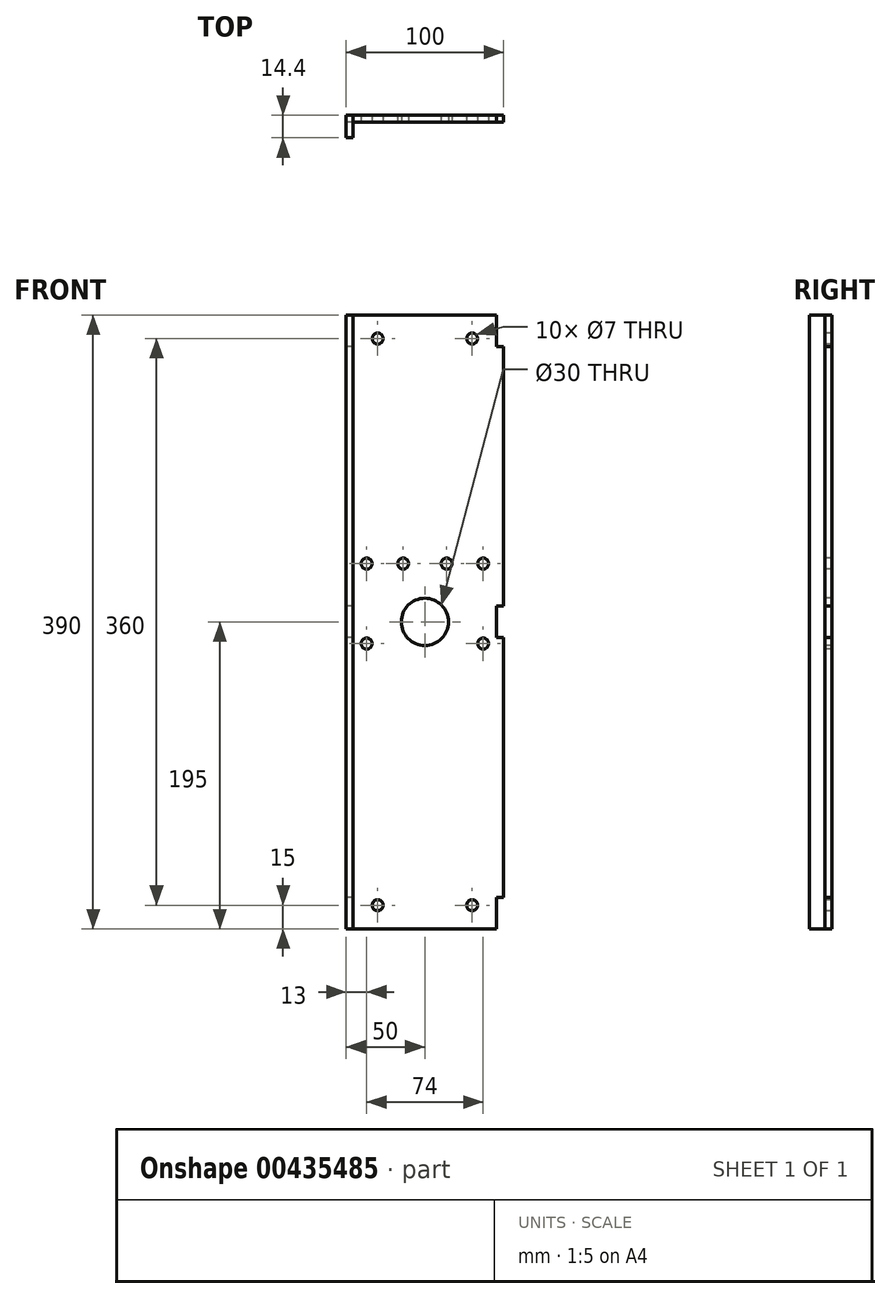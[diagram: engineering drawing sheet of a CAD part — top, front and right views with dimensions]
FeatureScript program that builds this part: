
annotation { "Feature Type Name" : "Feature", "Feature Type Description" : "" }
export const myFeature = defineFeature(function(context is Context, id is Id, definition is map)
    precondition{}
    {
        {
            assignVariable(context, id + "F0", {"name" : "t", "anyValue" : 4.4 * mm});
        }
        {
            var Q0;
            Q0=qCreatedBy(makeId("Front.planeOp"),FACE);
            var sketch = newSketch(context, id + "F1", { "sketchPlane" : qUnion([Q0])});
            skLineSegment(sketch, "E0", {"start": v(0, 0) * mm, "end": v(-45.6, 0) * mm});
            skLineSegment(sketch, "E1", {"start": v(-45.6, 0) * mm, "end": v(-45.6, 20) * mm});
            skLineSegment(sketch, "E2", {"start": v(-45.6, 20) * mm, "end": v(-50, 20) * mm});
            skLineSegment(sketch, "E3", {"start": v(-50, 20) * mm, "end": v(-50, 185) * mm});
            skLineSegment(sketch, "E4", {"start": v(-50, 185) * mm, "end": v(-45.6, 185) * mm});
            skLineSegment(sketch, "E5", {"start": v(-45.6, 185) * mm, "end": v(-45.6, 205) * mm});
            skLineSegment(sketch, "E6", {"start": v(-45.6, 205) * mm, "end": v(-50, 205) * mm});
            skLineSegment(sketch, "E7", {"start": v(-50, 205) * mm, "end": v(-50, 370) * mm});
            skLineSegment(sketch, "E8", {"start": v(-50, 370) * mm, "end": v(-45.6, 370) * mm});
            skLineSegment(sketch, "E9", {"start": v(-45.6, 370) * mm, "end": v(-45.6, 390) * mm});
            skLineSegment(sketch, "E10", {"start": v(-45.6, 390) * mm, "end": v(0, 390) * mm});
            skLineSegment(sketch, "E11", {"start": v(0, 390) * mm, "end": v(45.6, 390) * mm});
            skLineSegment(sketch, "E12", {"start": v(45.6, 390) * mm, "end": v(45.6, 370) * mm});
            skLineSegment(sketch, "E13", {"start": v(45.6, 370) * mm, "end": v(50, 370) * mm});
            skLineSegment(sketch, "E14", {"start": v(50, 370) * mm, "end": v(50, 205) * mm});
            skLineSegment(sketch, "E15", {"start": v(50, 205) * mm, "end": v(45.6, 205) * mm});
            skLineSegment(sketch, "E16", {"start": v(45.6, 205) * mm, "end": v(45.6, 185) * mm});
            skLineSegment(sketch, "E17", {"start": v(45.6, 185) * mm, "end": v(50, 185) * mm});
            skLineSegment(sketch, "E18", {"start": v(50, 185) * mm, "end": v(50, 20) * mm});
            skLineSegment(sketch, "E19", {"start": v(50, 20) * mm, "end": v(45.6, 20) * mm});
            skLineSegment(sketch, "E20", {"start": v(45.6, 20) * mm, "end": v(45.6, 0) * mm});
            skLineSegment(sketch, "E21", {"start": v(45.6, 0) * mm, "end": v(0, 0) * mm});
            skCircle(sketch, "E22", {"center": v(0, 195) * mm, "radius": 15 * mm});
            skLineSegment(sketch, "E23", {"start": v(0, 195) * mm, "end": v(37, 195) * mm, "construction": true});
            skLineSegment(sketch, "E24", {"start": v(37, 195) * mm, "end": v(37, 232) * mm, "construction": true});
            skCircle(sketch, "E25", {"center": v(37, 232) * mm, "radius": 3.5 * mm});
            skLineSegment(sketch, "E26", {"start": v(37, 232) * mm, "end": v(37, 181.2) * mm, "construction": true});
            skLineSegment(sketch, "E27", {"start": v(37, 232) * mm, "end": v(-13.8, 232) * mm, "construction": true});
            skCircle(sketch, "E28", {"center": v(37, 181.2) * mm, "radius": 3.5 * mm});
            skCircle(sketch, "E29", {"center": v(-13.8, 232) * mm, "radius": 3.5 * mm});
            skLineSegment(sketch, "E30", {"start": v(0, 195) * mm, "end": v(-37, 195) * mm, "construction": true});
            skLineSegment(sketch, "E31", {"start": v(-37, 195) * mm, "end": v(-37, 232) * mm, "construction": true});
            skCircle(sketch, "E32", {"center": v(-37, 232) * mm, "radius": 3.5 * mm});
            skLineSegment(sketch, "E33", {"start": v(-37, 232) * mm, "end": v(-37, 181.2) * mm, "construction": true});
            skLineSegment(sketch, "E34", {"start": v(-37, 232) * mm, "end": v(13.8, 232) * mm, "construction": true});
            skCircle(sketch, "E35", {"center": v(-37, 181.2) * mm, "radius": 3.5 * mm});
            skCircle(sketch, "E36", {"center": v(13.8, 232) * mm, "radius": 3.5 * mm});
            skLineSegment(sketch, "E37", {"start": v(0, 0) * mm, "end": v(0, 15) * mm});
            skLineSegment(sketch, "E38", {"start": v(0, 15) * mm, "end": v(30, 15) * mm, "construction": true});
            skLineSegment(sketch, "E39", {"start": v(0, 15) * mm, "end": v(-30, 15) * mm, "construction": true});
            skCircle(sketch, "E40", {"center": v(30, 15) * mm, "radius": 3.5 * mm});
            skCircle(sketch, "E41", {"center": v(-30, 15) * mm, "radius": 3.5 * mm});
            skLineSegment(sketch, "E42", {"start": v(0, 390) * mm, "end": v(0, 375) * mm, "construction": true});
            skLineSegment(sketch, "E43", {"start": v(0, 375) * mm, "end": v(30, 375) * mm, "construction": true});
            skLineSegment(sketch, "E44", {"start": v(0, 375) * mm, "end": v(-30, 375) * mm, "construction": true});
            skCircle(sketch, "E45", {"center": v(30, 375) * mm, "radius": 3.5 * mm});
            skCircle(sketch, "E46", {"center": v(-30, 375) * mm, "radius": 3.5 * mm});
            skLineSegment(sketch, "E47", {"start": v(0, 0) * mm, "end": v(0, 195) * mm});
            skLineSegment(sketch, "E48", {"start": v(-45.6, 390) * mm, "end": v(-45.6, 0) * mm, "construction": true});
            skSolve(sketch);
        }
        {
            var Q0;
            Q0=makeQuery(id+"F1.imprint","IMPRINT",FACE,{"disambiguationData":[TD([[makeQuery(id+"F1.imprint","IMPRINT",EDGE,{"derivedFrom":sQuery(id+"F1.wireOp",EDGE,"E0")}),-1.0]])]});
            extrude(context, id + "F2", {"entities" : qUnion([Q0]), "oppositeDirection" : true, "depth" : getVariable(context, 't')});
        }
        {
            var Q0;
            Q0=makeQuery(id+"F2.opExtrude","SWEPT_FACE",FACE,{"disambiguationData":[OSD([sQuery(id+"F1.wireOp",EDGE,"E7")])]});
            var sketch = newSketch(context, id + "F3", { "sketchPlane" : qUnion([Q0])});
            skLineSegment(sketch, "E49", {"start": v(-4.4, 370) * mm, "end": v(-4.4, 390) * mm});
            skLineSegment(sketch, "E50", {"start": v(-4.4, 390) * mm, "end": v(10, 390) * mm});
            skLineSegment(sketch, "E51", {"start": v(-4.4, 370) * mm, "end": v(0, 370) * mm});
            skPoint(sketch, "E51.endSnap0", {"position": v(-2.2, 370) * mm});
            skLineSegment(sketch, "E52", {"start": v(0, 205) * mm, "end": v(-4.4, 205) * mm});
            skLineSegment(sketch, "E53", {"start": v(-4.4, 205) * mm, "end": v(-4.4, 185) * mm});
            skLineSegment(sketch, "E54", {"start": v(-4.4, 185) * mm, "end": v(0, 185) * mm});
            skLineSegment(sketch, "E55", {"start": v(0, 205) * mm, "end": v(0, 370) * mm});
            skLineSegment(sketch, "E56", {"start": v(0, 0) * mm, "end": v(10, 0) * mm});
            skLineSegment(sketch, "E57", {"start": v(0, 0) * mm, "end": v(-4.4, 0) * mm});
            skLineSegment(sketch, "E58", {"start": v(-4.4, 0) * mm, "end": v(-4.4, 20) * mm});
            skLineSegment(sketch, "E59", {"start": v(-4.4, 20) * mm, "end": v(0, 20) * mm});
            skLineSegment(sketch, "E60", {"start": v(0, 20) * mm, "end": v(0, 185) * mm});
            skLineSegment(sketch, "E61", {"start": v(10, 0) * mm, "end": v(10, 390) * mm});
            skSolve(sketch);
        }
        {
            var Q0;
            Q0=makeQuery(id+"F3.imprint","IMPRINT",FACE,{"disambiguationData":[TD([[makeQuery(id+"F3.imprint","IMPRINT",EDGE,{"derivedFrom":sQuery(id+"F3.wireOp",EDGE,"E49")}),-1.0]])]});
            extrude(context, id + "F4", {"entities" : qUnion([Q0]), "oppositeDirection" : true, "depth" : getVariable(context, 't')});
        }
    });
